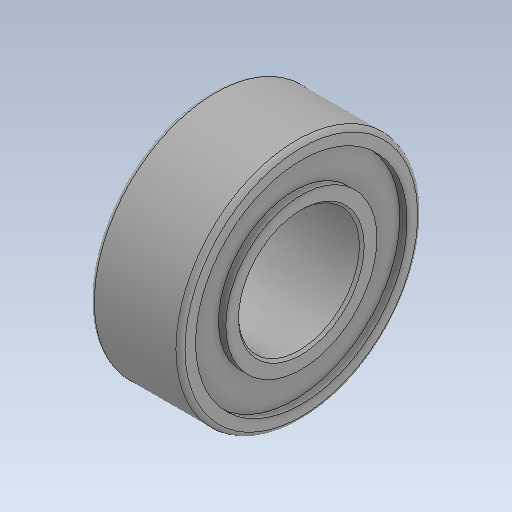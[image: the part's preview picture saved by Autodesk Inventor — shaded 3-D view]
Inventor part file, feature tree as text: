
AUTODESK INVENTOR PART (.ipt)
format: ipt  version: 2020 (Build 240168000, 168)  size: 172,032 bytes
history: native  units: in
note: dims shown in document units (in); Inventor stores cm internally (conversion verified against a paired STEP export)
features: chamfer x1
ambient origin geometry x8: Origin, YZ Plane, XZ Plane, XY Plane, X Axis, Y Axis, Z Axis, Center Point
bodies: Solid1 (feature_tree)
feature tree (1):
  chamfer  "Chamfer1"  [1 undecoded]
note: 1 required parameter value undecoded (feature->parameter linkage not recoverable at this tier; creation-order binding heuristic only, values carry confidence <= 0.55)
